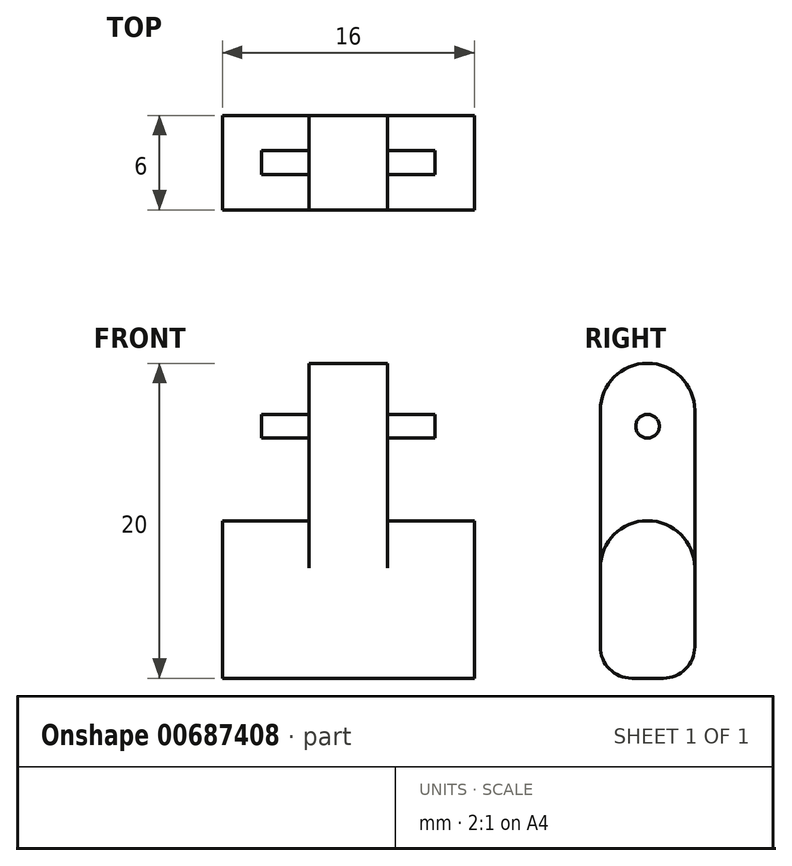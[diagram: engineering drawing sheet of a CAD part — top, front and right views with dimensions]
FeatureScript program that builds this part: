
annotation { "Feature Type Name" : "Feature", "Feature Type Description" : "" }
export const myFeature = defineFeature(function(context is Context, id is Id, definition is map)
    precondition{}
    {
        {
            var Q0;
            Q0=qCreatedBy(makeId("Front.planeOp"),FACE);
            var sketch = newSketch(context, id + "F0", { "sketchPlane" : qUnion([Q0])});
            skLineSegment(sketch, "E0", {"start": v(0, 0) * mm, "end": v(0, -10) * mm});
            skLineSegment(sketch, "E1", {"start": v(0, -10) * mm, "end": v(16, -10) * mm});
            skLineSegment(sketch, "E2", {"start": v(16, -10) * mm, "end": v(16, 0) * mm});
            skLineSegment(sketch, "E3", {"start": v(16, 0) * mm, "end": v(10.5, 0) * mm});
            skLineSegment(sketch, "E4", {"start": v(10.5, 10) * mm, "end": v(10.5, 0) * mm});
            skLineSegment(sketch, "E5", {"start": v(10.5, 10) * mm, "end": v(5.5, 10) * mm});
            skLineSegment(sketch, "E6", {"start": v(5.5, 0) * mm, "end": v(5.5, 10) * mm});
            skLineSegment(sketch, "E7", {"start": v(5.5, 0) * mm, "end": v(0, 0) * mm});
            skSolve(sketch);
        }
        {
            var Q0;
            Q0=makeQuery(id+"F0.imprint","IMPRINT",FACE,{"disambiguationData":[TD([[makeQuery(id+"F0.imprint","IMPRINT",EDGE,{"derivedFrom":sQuery(id+"F0.wireOp",EDGE,"E0")}),1.0]])]});
            extrude(context, id + "F1", {"entities" : qUnion([Q0]), "depth" : 6 * mm, "offsetDistance" : 25 * mm});
        }
        {
            var Q0;
            Q0=makeQuery(id+"F1.opExtrude","SWEPT_FACE",FACE,{"disambiguationData":[OSD([sQuery(id+"F0.wireOp",EDGE,"E4")])]});
            var sketch = newSketch(context, id + "F2", { "sketchPlane" : qUnion([Q0])});
            skCircle(sketch, "E8", {"center": v(-3, 6) * mm, "radius": 0.75 * mm});
            skSolve(sketch);
        }
        {
            var Q0;
            Q0 = qSketchRegion(id + "F2", true);
            extrude(context, id + "F3", {"entities" : qUnion([Q0]), "operationType" : NewBodyOperationType.ADD, "depth" : (3) * mm, "offsetDistance" : 25 * mm, "hasSecondDirection" : true, "secondDirectionOppositeDirection" : true, "secondDirectionDepth" : 8 * mm});
        }
        {
            var Q0;
            Q0=makeQuery(id+"F1.opExtrude","CAP_EDGE",EDGE,{"disambiguationData":[OSD([sQuery(id+"F0.wireOp",EDGE,"E5")])],"isStart":false});
            var Q1;
            Q1=makeQuery(id+"F1.opExtrude","CAP_EDGE",EDGE,{"disambiguationData":[OSD([sQuery(id+"F0.wireOp",EDGE,"E5")])],"isStart":true});
            fillet(context, id + "F4", {"entities" : qUnion([Q0, Q1]), "radius" : 3 * mm, "tangentPropagation" : true, "allowEdgeOverflow" : false});
        }
        {
            var Q0;
            Q0=makeQuery(id+"F1.opExtrude","CAP_EDGE",EDGE,{"disambiguationData":[OSD([sQuery(id+"F0.wireOp",EDGE,"E7")])],"isStart":false});
            var Q1;
            Q1=makeQuery(id+"F1.opExtrude","CAP_EDGE",EDGE,{"disambiguationData":[OSD([sQuery(id+"F0.wireOp",EDGE,"E7")])],"isStart":true});
            var Q2;
            Q2=makeQuery(id+"F1.opExtrude","CAP_EDGE",EDGE,{"disambiguationData":[OSD([sQuery(id+"F0.wireOp",EDGE,"E3")])],"isStart":false});
            var Q3;
            Q3=makeQuery(id+"F1.opExtrude","CAP_EDGE",EDGE,{"disambiguationData":[OSD([sQuery(id+"F0.wireOp",EDGE,"E3")])],"isStart":true});
            fillet(context, id + "F5", {"entities" : qUnion([Q0, Q1, Q2, Q3]), "radius" : 3 * mm, "tangentPropagation" : true, "allowEdgeOverflow" : false});
        }
        {
            var Q0;
            Q0=makeQuery(id+"F1.opExtrude","CAP_EDGE",EDGE,{"disambiguationData":[OSD([sQuery(id+"F0.wireOp",EDGE,"E1")])],"isStart":false});
            var Q1;
            Q1=makeQuery(id+"F1.opExtrude","CAP_EDGE",EDGE,{"disambiguationData":[OSD([sQuery(id+"F0.wireOp",EDGE,"E1")])],"isStart":true});
            fillet(context, id + "F6", {"entities" : qUnion([Q0, Q1]), "radius" : 2 * mm, "tangentPropagation" : true, "allowEdgeOverflow" : false});
        }
    });
